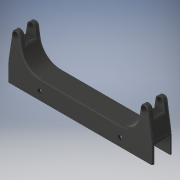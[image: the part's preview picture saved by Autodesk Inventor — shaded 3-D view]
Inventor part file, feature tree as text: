
AUTODESK INVENTOR PART (.ipt)
format: ipt  version: 2019.4 (Build 234330000, 330)  size: 245,248 bytes
history: native  units: mm
features: extrude x4, fillet x4, sketch x2, hole x2
ambient origin geometry x8: Origin, YZ Plane, XZ Plane, XY Plane, X Axis, Y Axis, Z Axis, Center Point
bodies: Solid1 (feature_tree)
feature tree (12):
  sketch  "Sketch1"  dims[d0=180.0mm d1=55.0mm]
  extrude  "Extrusion1"  Depth=55.0mm
  extrude  "Extrusion2"  Depth=1.5mm
  extrude  "Extrusion3"  Depth=1.5mm
  hole  "Hole1"  [1 undecoded]
  extrude  "Extrusion4"  Depth=10.0mm
  hole  "Hole2"  [1 undecoded]
  fillet  "Fillet2"  Radius=180.0mm
  fillet  "Fillet3"  Radius=2.5mm
  fillet  "Fillet4"  Radius=10.0mm
  fillet  "Fillet5"  Radius=10.0mm
  sketch  "Sketch2"  dims[d2=180.0mm d3=20.0mm d4=160.0mm d5=10.0mm d6=10.0mm d7=10.0mm d10=180.0mm d11=2.5mm d12=10.0mm d13=10.0mm d14=25.0mm d15=0.0mm d16=25.0mm d17=0.0mm d18=22.0mm d19=22.0mm d20=14.0mm d21=0.0mm d22=8.0mm d23=6.0mm d24=4.0mm d25=2.0mm d26=90.0deg d27=8.0mm d28=20.594885mm d29=20.0mm d30=2.5mm d31=2.5mm d32=180.0mm d33=0.0mm d34=50.0mm d35=100.0mm d36=5.0mm d37=6.0mm d38=4.0mm d39=2.0mm d40=90.0deg d41=8.0mm d42=20.594885mm d44=25.0mm d45=20.0mm d48=25.0mm d49=1.5mm d50=1.5mm]
note: 2 required parameter values undecoded (feature->parameter linkage not recoverable at this tier; creation-order binding heuristic only, values carry confidence <= 0.55)
